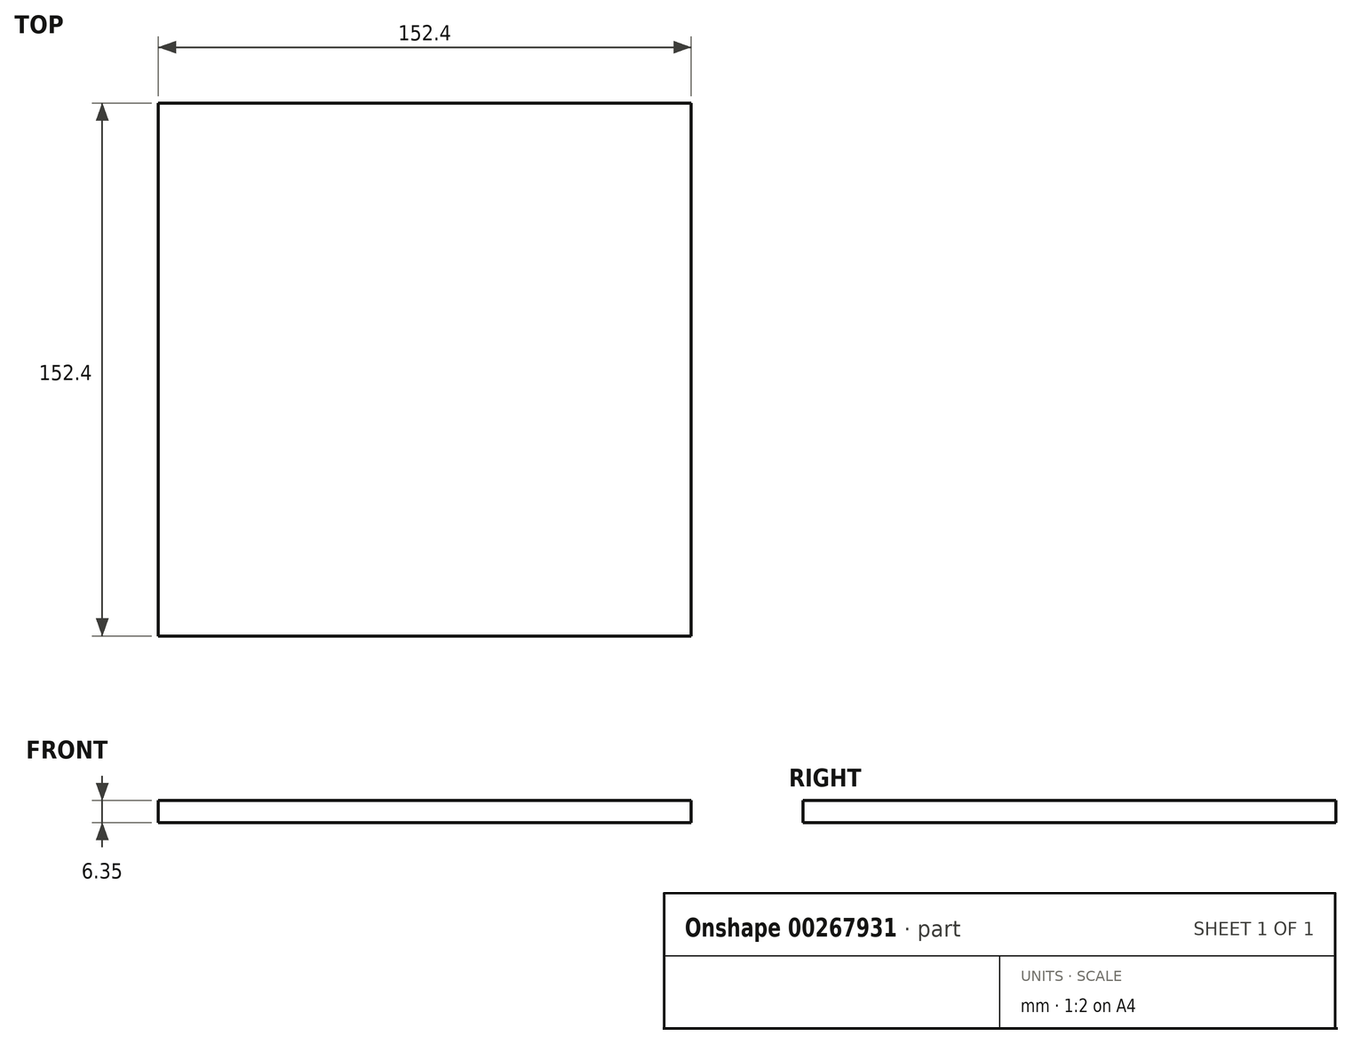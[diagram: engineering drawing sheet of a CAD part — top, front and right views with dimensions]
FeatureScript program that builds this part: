
annotation { "Feature Type Name" : "Feature", "Feature Type Description" : "" }
export const myFeature = defineFeature(function(context is Context, id is Id, definition is map)
    precondition{}
    {
        {
            var Q0;
            Q0=qCreatedBy(makeId("Top.planeOp"),FACE);
            var sketch = newSketch(context, id + "F0", { "sketchPlane" : qUnion([Q0])});
            skLineSegment(sketch, "E0.bottom", {"start": v(-76.2, 76.2) * mm, "end": v(76.2, 76.2) * mm});
            skLineSegment(sketch, "E0.top", {"start": v(-76.2, -76.2) * mm, "end": v(76.2, -76.2) * mm});
            skLineSegment(sketch, "E0.left", {"start": v(-76.2, 76.2) * mm, "end": v(-76.2, -76.2) * mm});
            skLineSegment(sketch, "E0.right", {"start": v(76.2, 76.2) * mm, "end": v(76.2, -76.2) * mm});
            skPoint(sketch, "E0.middle", {"position": v(0, 0) * mm});
            skLineSegment(sketch, "E1.bottom", {"start": v(-88.9, 88.9) * mm, "end": v(88.9, 88.9) * mm});
            skLineSegment(sketch, "E1.top", {"start": v(-88.9, -88.9) * mm, "end": v(88.9, -88.9) * mm});
            skLineSegment(sketch, "E1.left", {"start": v(-88.9, 88.9) * mm, "end": v(-88.9, -88.9) * mm});
            skLineSegment(sketch, "E1.right", {"start": v(88.9, 88.9) * mm, "end": v(88.9, -88.9) * mm});
            skLineSegment(sketch, "E2.bottom", {"start": v(-82.55, 82.55) * mm, "end": v(82.55, 82.55) * mm, "construction": true});
            skLineSegment(sketch, "E2.top", {"start": v(-82.55, -82.55) * mm, "end": v(82.55, -82.55) * mm, "construction": true});
            skLineSegment(sketch, "E2.left", {"start": v(-82.55, 82.55) * mm, "end": v(-82.55, -82.55) * mm, "construction": true});
            skLineSegment(sketch, "E2.right", {"start": v(82.55, 82.55) * mm, "end": v(82.55, -82.55) * mm, "construction": true});
            skCircle(sketch, "E3", {"center": v(-82.55, 82.55) * mm, "radius": 2.55 * mm});
            skCircle(sketch, "E4", {"center": v(82.55, 82.55) * mm, "radius": 2.55 * mm});
            skCircle(sketch, "E5", {"center": v(-82.55, -82.55) * mm, "radius": 2.55 * mm});
            skCircle(sketch, "E6", {"center": v(82.55, -82.55) * mm, "radius": 2.55 * mm});
            skSolve(sketch);
        }
        {
            var Q0;
            Q0=makeQuery(id+"F0.imprint","IMPRINT",FACE,{"disambiguationData":[TD([[makeQuery(id+"F0.imprint","IMPRINT",EDGE,{"derivedFrom":sQuery(id+"F0.wireOp",EDGE,"E0.bottom")}),-1.0]])]});
            extrude(context, id + "F1", {"entities" : qUnion([Q0]), "depth" : 6.35 * mm, "offsetDistance" : 25.4 * mm});
        }
    });
